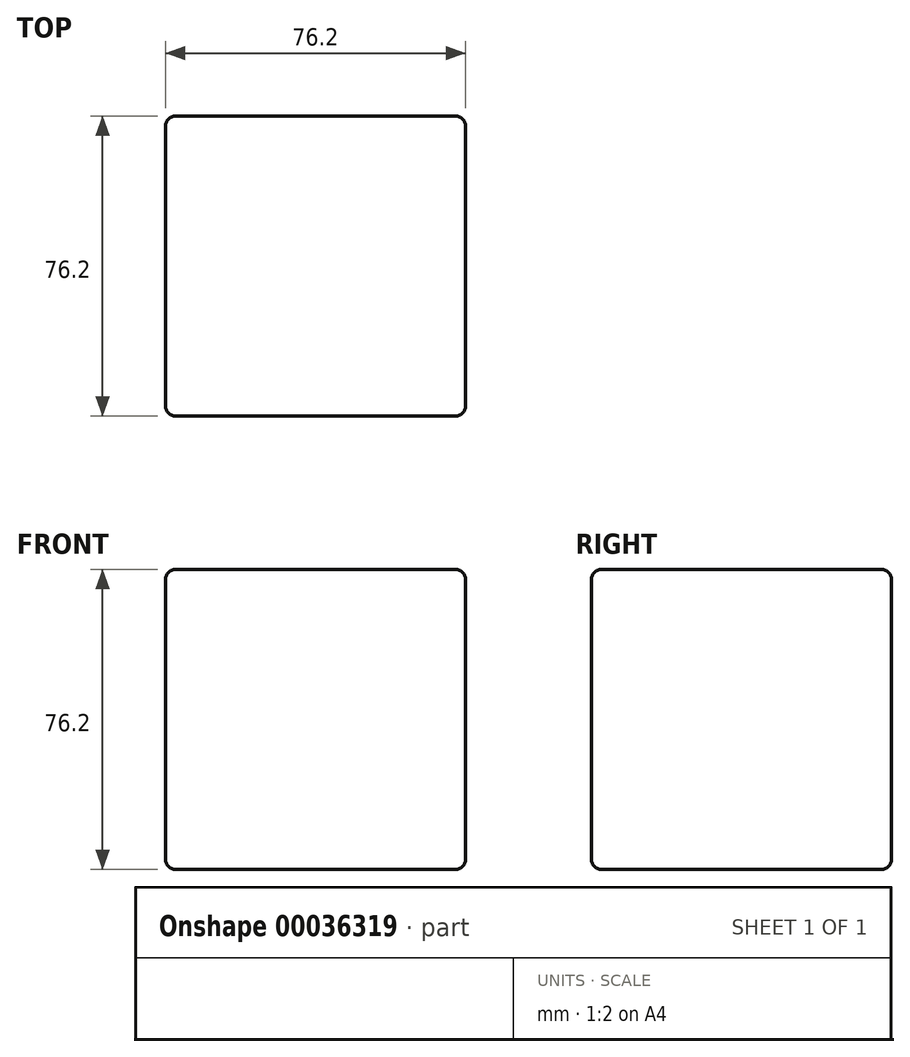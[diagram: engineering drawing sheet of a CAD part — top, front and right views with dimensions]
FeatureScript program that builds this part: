
annotation { "Feature Type Name" : "Feature", "Feature Type Description" : "" }
export const myFeature = defineFeature(function(context is Context, id is Id, definition is map)
    precondition{}
    {
        {
            var Q0;
            Q0=qCreatedBy(makeId("Top.planeOp"),FACE);
            var sketch = newSketch(context, id + "F0", { "sketchPlane" : qUnion([Q0])});
            skLineSegment(sketch, "E0.bottom", {"start": v(-38.1, 38.1) * mm, "end": v(38.1, 38.1) * mm});
            skLineSegment(sketch, "E0.top", {"start": v(-38.1, -38.1) * mm, "end": v(38.1, -38.1) * mm});
            skLineSegment(sketch, "E0.left", {"start": v(-38.1, 38.1) * mm, "end": v(-38.1, -38.1) * mm});
            skLineSegment(sketch, "E0.right", {"start": v(38.1, 38.1) * mm, "end": v(38.1, -38.1) * mm});
            skSolve(sketch);
        }
        {
            var Q0;
            Q0 = qSketchRegion(id + "F0", true);
            extrude(context, id + "F1", {"entities" : qUnion([Q0]), "depth" : 76.2 * mm});
        }
        {
            var Q0;
            Q0=makeQuery(id+"F1.opExtrude","CAP_EDGE",EDGE,{"disambiguationData":[OSD([sQuery(id+"F0.wireOp",EDGE,"E0.right")])],"isStart":false});
            var Q1;
            Q1=makeQuery(id+"F1.opExtrude","CAP_EDGE",EDGE,{"disambiguationData":[OSD([sQuery(id+"F0.wireOp",EDGE,"E0.top")])],"isStart":false});
            var Q2;
            Q2=makeQuery(id+"F1.opExtrude","CAP_EDGE",EDGE,{"disambiguationData":[OSD([sQuery(id+"F0.wireOp",EDGE,"E0.left")])],"isStart":false});
            var Q3;
            Q3=makeQuery(id+"F1.opExtrude","CAP_EDGE",EDGE,{"disambiguationData":[OSD([sQuery(id+"F0.wireOp",EDGE,"E0.bottom")])],"isStart":false});
            var Q4;
            Q4=makeQuery(id+"F1.opExtrude","SWEPT_EDGE",EDGE,{"disambiguationData":[OSD([sQuery(id+"F0.wireOp",EDGE,"E0.top"),sQuery(id+"F0.wireOp",EDGE,"E0.right")])]});
            var Q5;
            Q5=makeQuery(id+"F1.opExtrude","SWEPT_EDGE",EDGE,{"disambiguationData":[OSD([sQuery(id+"F0.wireOp",EDGE,"E0.bottom"),sQuery(id+"F0.wireOp",EDGE,"E0.right")])]});
            var Q6;
            Q6=makeQuery(id+"F1.opExtrude","SWEPT_EDGE",EDGE,{"disambiguationData":[OSD([sQuery(id+"F0.wireOp",EDGE,"E0.top"),sQuery(id+"F0.wireOp",EDGE,"E0.left")])]});
            var Q7;
            Q7=makeQuery(id+"F1.opExtrude","CAP_EDGE",EDGE,{"disambiguationData":[OSD([sQuery(id+"F0.wireOp",EDGE,"E0.left")])],"isStart":true});
            var Q8;
            Q8=makeQuery(id+"F1.opExtrude","CAP_EDGE",EDGE,{"disambiguationData":[OSD([sQuery(id+"F0.wireOp",EDGE,"E0.top")])],"isStart":true});
            var Q9;
            Q9=makeQuery(id+"F1.opExtrude","CAP_EDGE",EDGE,{"disambiguationData":[OSD([sQuery(id+"F0.wireOp",EDGE,"E0.right")])],"isStart":true});
            var Q10;
            Q10=makeQuery(id+"F1.opExtrude","CAP_EDGE",EDGE,{"disambiguationData":[OSD([sQuery(id+"F0.wireOp",EDGE,"E0.bottom")])],"isStart":true});
            var Q11;
            Q11=makeQuery(id+"F1.opExtrude","SWEPT_EDGE",EDGE,{"disambiguationData":[OSD([sQuery(id+"F0.wireOp",EDGE,"E0.bottom"),sQuery(id+"F0.wireOp",EDGE,"E0.left")])]});
            fillet(context, id + "F2", {"entities" : qUnion([Q0, Q1, Q2, Q3, Q4, Q5, Q6, Q7, Q8, Q9, Q10, Q11]), "radius" : 2.54 * mm, "tangentPropagation" : true, "allowEdgeOverflow" : false});
        }
    });
